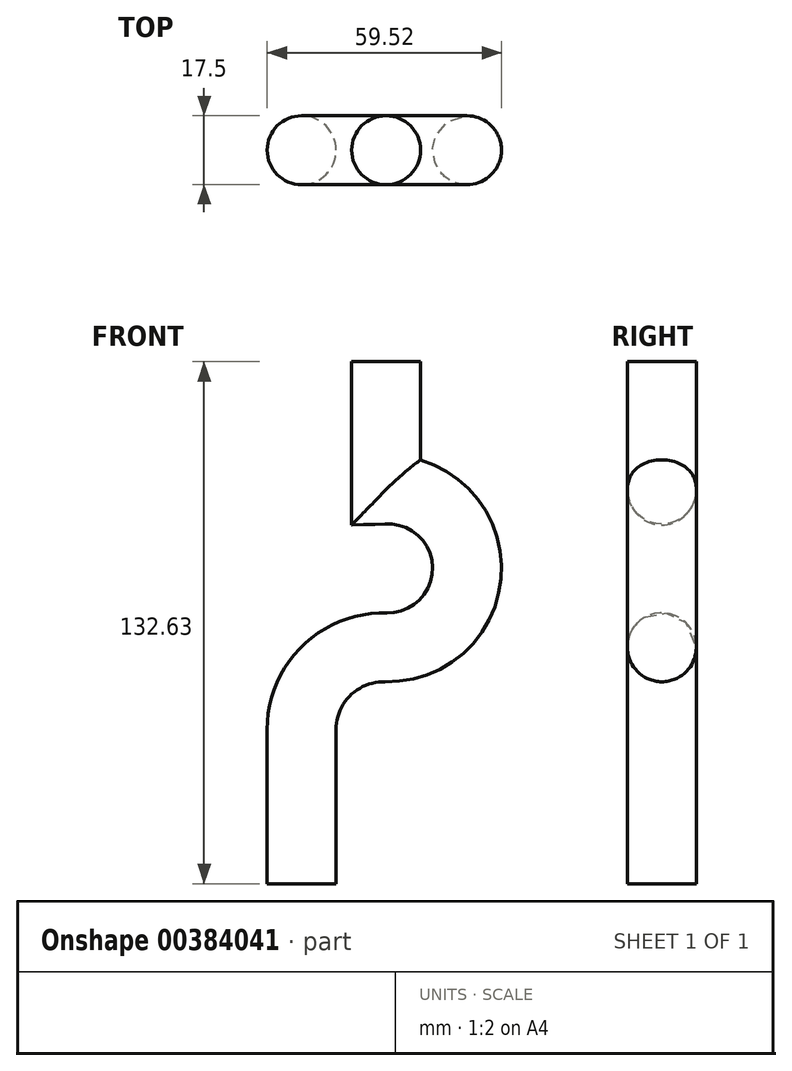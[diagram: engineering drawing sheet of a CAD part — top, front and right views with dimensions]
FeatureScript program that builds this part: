
annotation { "Feature Type Name" : "Feature", "Feature Type Description" : "" }
export const myFeature = defineFeature(function(context is Context, id is Id, definition is map)
    precondition{}
    {
        {
            var Q0;
            Q0=qCreatedBy(makeId("Top.planeOp"),FACE);
            var sketch = newSketch(context, id + "F0", { "sketchPlane" : qUnion([Q0])});
            skCircle(sketch, "E0", {"center": v(0, 0) * mm, "radius": 8.75 * mm});
            skSolve(sketch);
        }
        {
            var Q0;
            Q0=qCreatedBy(makeId("Front.planeOp"),FACE);
            var sketch = newSketch(context, id + "F1", { "sketchPlane" : qUnion([Q0])});
            skLineSegment(sketch, "E1", {"start": v(0, 0) * mm, "end": v(0, 39.16) * mm});
            skArc(sketch, "E2", {"start": v(0, 39.16) * mm, "mid": v(6.32, 54.15) * mm, "end": v(21.47, 60.09) * mm});
            skArc(sketch, "E3", {"start": v(21.47, 60.09) * mm, "mid": v(42.02, 80.12) * mm, "end": v(21.47, 100.15) * mm});
            skLineSegment(sketch, "E4", {"start": v(21.47, 100.15) * mm, "end": v(21.47, 132.63) * mm});
            skSolve(sketch);
        }
        {
            var Q0;
            Q0 = qSketchRegion(id + "F0", true);
            var Q1;
            Q1 = qBodyType(qCreatedBy(id + "F1" ,EDGE), BodyType.WIRE);
            sweep(context, id + "F2", {"profiles" : qUnion([Q0]), "path" : qUnion([Q1])});
        }
    });
